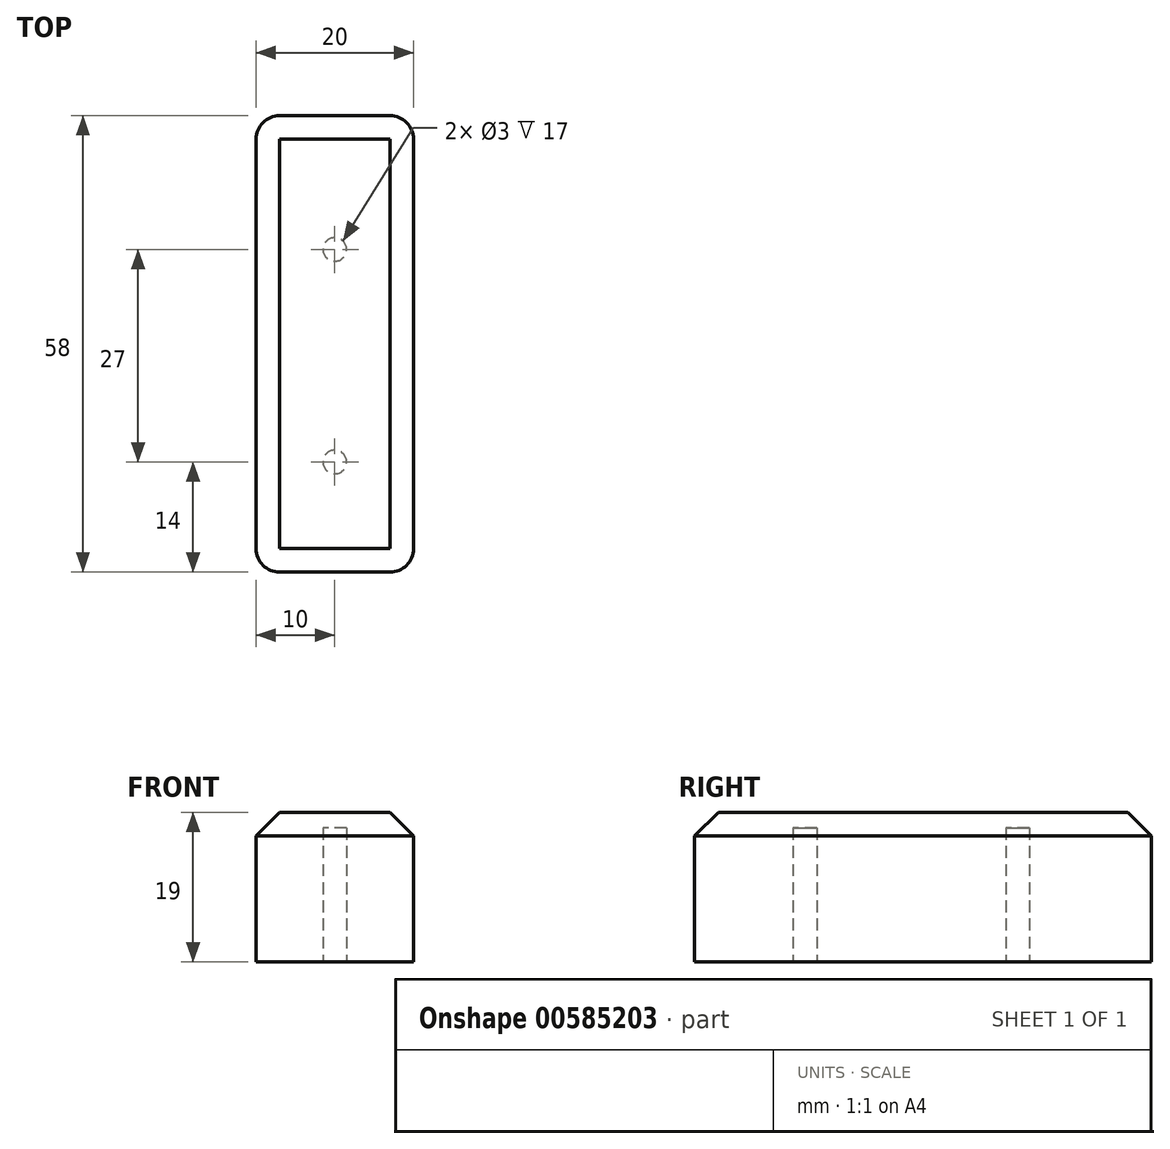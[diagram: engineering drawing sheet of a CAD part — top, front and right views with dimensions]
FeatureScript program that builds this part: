
annotation { "Feature Type Name" : "Feature", "Feature Type Description" : "" }
export const myFeature = defineFeature(function(context is Context, id is Id, definition is map)
    precondition{}
    {
        {
            var Q0;
            Q0=qCreatedBy(makeId("Top.planeOp"),FACE);
            var sketch = newSketch(context, id + "F0", { "sketchPlane" : qUnion([Q0])});
            skLineSegment(sketch, "E0.bottom", {"start": v(-10, 29) * mm, "end": v(10, 29) * mm});
            skLineSegment(sketch, "E0.top", {"start": v(-10, -29) * mm, "end": v(10, -29) * mm});
            skLineSegment(sketch, "E0.left", {"start": v(-10, 29) * mm, "end": v(-10, -29) * mm});
            skLineSegment(sketch, "E0.right", {"start": v(10, 29) * mm, "end": v(10, -29) * mm});
            skPoint(sketch, "E0.middle", {"position": v(0, 0) * mm});
            skSolve(sketch);
        }
        {
            var Q0;
            Q0 = qSketchRegion(id + "F0", true);
            extrude(context, id + "F1", {"entities" : qUnion([Q0]), "depth" : 19 * mm, "offsetDistance" : 25 * mm});
        }
        {
            var Q0;
            Q0=qCreatedBy(makeId("Top.planeOp"),FACE);
            var sketch = newSketch(context, id + "F2", { "sketchPlane" : qUnion([Q0])});
            skCircle(sketch, "E1", {"center": v(0, 12) * mm, "radius": 1.5 * mm});
            skCircle(sketch, "E2", {"center": v(0, -15) * mm, "radius": 1.5 * mm});
            skSolve(sketch);
        }
        {
            var Q0;
            Q0 = qSketchRegion(id + "F2", true);
            extrude(context, id + "F3", {"entities" : qUnion([Q0]), "operationType" : NewBodyOperationType.REMOVE, "depth" : 17 * mm, "offsetDistance" : 25 * mm});
        }
        {
            var Q0;
            Q0=makeQuery(id+"F1.opExtrude","SWEPT_EDGE",EDGE,{"disambiguationData":[OSD([sQuery(id+"F0.wireOp",EDGE,"E0.bottom"),sQuery(id+"F0.wireOp",EDGE,"E0.left")])]});
            var Q1;
            Q1=makeQuery(id+"F1.opExtrude","SWEPT_EDGE",EDGE,{"disambiguationData":[OSD([sQuery(id+"F0.wireOp",EDGE,"E0.bottom"),sQuery(id+"F0.wireOp",EDGE,"E0.right")])]});
            var Q2;
            Q2=makeQuery(id+"F1.opExtrude","SWEPT_EDGE",EDGE,{"disambiguationData":[OSD([sQuery(id+"F0.wireOp",EDGE,"E0.top"),sQuery(id+"F0.wireOp",EDGE,"E0.left")])]});
            var Q3;
            Q3=makeQuery(id+"F1.opExtrude","SWEPT_EDGE",EDGE,{"disambiguationData":[OSD([sQuery(id+"F0.wireOp",EDGE,"E0.top"),sQuery(id+"F0.wireOp",EDGE,"E0.right")])]});
            fillet(context, id + "F4", {"entities" : qUnion([Q0, Q1, Q2, Q3]), "radius" : 3 * mm, "tangentPropagation" : true, "allowEdgeOverflow" : false});
        }
        {
            var Q0;
            Q0=makeQuery(id+"F1.opExtrude","CAP_EDGE",EDGE,{"disambiguationData":[OSD([sQuery(id+"F0.wireOp",EDGE,"E0.left")])],"isStart":false});
            chamfer(context, id + "F5", {"entities" : qUnion([Q0]), "width" : 3 * mm, "tangentPropagation" : true});
        }
    });
